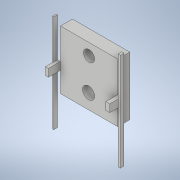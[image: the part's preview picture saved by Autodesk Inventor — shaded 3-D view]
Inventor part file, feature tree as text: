
AUTODESK INVENTOR PART (.ipt)
format: ipt  version: 2021 (Build 250183000, 183)  size: 143,872 bytes
history: native  units: in
note: dims shown in document units (in); Inventor stores cm internally (conversion verified against a paired STEP export)
features: extrude x3, sketch x3, other x1
ambient origin geometry x8: Origin, YZ Plane, XZ Plane, XY Plane, X Axis, Y Axis, Z Axis, Center Point
bodies: Solid1 (feature_tree)
feature tree (7):
  extrude  "Extrusion1"  Depth=1.0in TaperAngle=0.0deg
  extrude  "Extrusion2"  Depth=0.3in TaperAngle=0.0deg
  extrude  "Extrusion3"  [1 undecoded]
  other  "Move Face1"
  sketch  "Sketch1"  dims[d0=1.0in d1=1.0in d2=0.0in]
  sketch  "Sketch2"  dims[d3=1.0in d4=0.0in d6=0.3in d7=0.0in]
  sketch  "Sketch3"
note: 1 required parameter value undecoded (feature->parameter linkage not recoverable at this tier; creation-order binding heuristic only, values carry confidence <= 0.55)
